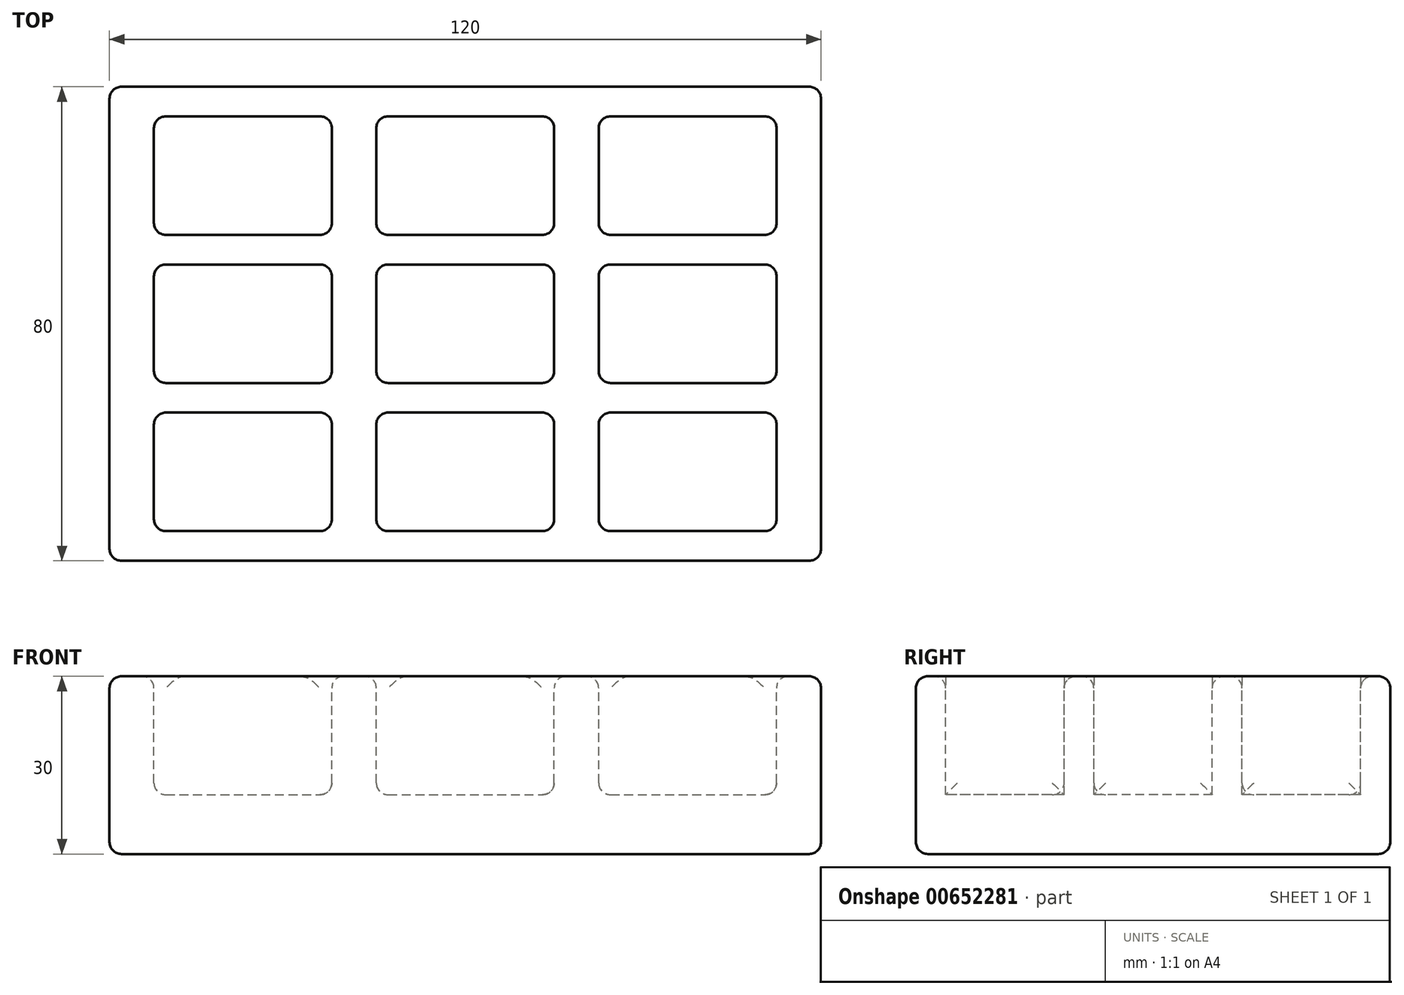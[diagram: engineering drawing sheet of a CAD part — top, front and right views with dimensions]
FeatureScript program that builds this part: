
annotation { "Feature Type Name" : "Feature", "Feature Type Description" : "" }
export const myFeature = defineFeature(function(context is Context, id is Id, definition is map)
    precondition{}
    {
        {
            var Q0;
            Q0=qCreatedBy(makeId("Top.planeOp"),FACE);
            var sketch = newSketch(context, id + "F0", { "sketchPlane" : qUnion([Q0])});
            skLineSegment(sketch, "E0.bottom", {"start": v(60, -40) * mm, "end": v(-60, -40) * mm});
            skLineSegment(sketch, "E0.top", {"start": v(60, 40) * mm, "end": v(-60, 40) * mm});
            skLineSegment(sketch, "E0.left", {"start": v(60, -40) * mm, "end": v(60, 40) * mm});
            skLineSegment(sketch, "E0.right", {"start": v(-60, -40) * mm, "end": v(-60, 40) * mm});
            skPoint(sketch, "E0.middle", {"position": v(0, 0) * mm});
            skSolve(sketch);
        }
        {
            var Q0;
            Q0 = qSketchRegion(id + "F0", true);
            extrude(context, id + "F1", {"entities" : qUnion([Q0]), "depth" : 30 * mm, "offsetDistance" : 25 * mm});
        }
        {
            var Q0;
            Q0=makeQuery(id+"F1.opExtrude","CAP_FACE",FACE,{"disambiguationData":[OSD([sQuery(id+"F0.wireOp",EDGE,"E0.bottom"),sQuery(id+"F0.wireOp",EDGE,"E0.top"),sQuery(id+"F0.wireOp",EDGE,"E0.left"),sQuery(id+"F0.wireOp",EDGE,"E0.right")])],"isStart":false});
            var sketch = newSketch(context, id + "F2", { "sketchPlane" : qUnion([Q0])});
            skLineSegment(sketch, "E1.bottom", {"start": v(-52.5, 35) * mm, "end": v(-22.5, 35) * mm});
            skLineSegment(sketch, "E1.top", {"start": v(-52.5, 15) * mm, "end": v(-22.5, 15) * mm});
            skLineSegment(sketch, "E1.left", {"start": v(-52.5, 35) * mm, "end": v(-52.5, 15) * mm});
            skLineSegment(sketch, "E1.right", {"start": v(-22.5, 35) * mm, "end": v(-22.5, 15) * mm});
            skLineSegment(sketch, "E2", {"start": v(-22.5, 35) * mm, "end": v(60, 35) * mm, "construction": true});
            skLineSegment(sketch, "E3", {"start": v(-22.5, -40) * mm, "end": v(-22.5, 35) * mm, "construction": true});
            skLineSegment(sketch, "E4", {"start": v(-22.5, 15) * mm, "end": v(60, 15) * mm, "construction": true});
            skLineSegment(sketch, "E5", {"start": v(-15, 35) * mm, "end": v(-15, -40) * mm, "construction": true});
            skLineSegment(sketch, "E6", {"start": v(52.5, 35) * mm, "end": v(52.5, -40) * mm, "construction": true});
            skLineSegment(sketch, "E7.bottom", {"start": v(-15, 35) * mm, "end": v(15, 35) * mm});
            skLineSegment(sketch, "E7.top", {"start": v(-15, 15) * mm, "end": v(15, 15) * mm});
            skLineSegment(sketch, "E7.left", {"start": v(-15, 35) * mm, "end": v(-15, 15) * mm});
            skLineSegment(sketch, "E7.right", {"start": v(15, 35) * mm, "end": v(15, 15) * mm});
            skLineSegment(sketch, "E8.bottom", {"start": v(52.5, 35) * mm, "end": v(22.5, 35) * mm});
            skLineSegment(sketch, "E8.top", {"start": v(52.5, 15) * mm, "end": v(22.5, 15) * mm});
            skLineSegment(sketch, "E8.left", {"start": v(52.5, 35) * mm, "end": v(52.5, 15) * mm});
            skLineSegment(sketch, "E8.right", {"start": v(22.5, 35) * mm, "end": v(22.5, 15) * mm});
            skLineSegment(sketch, "E9", {"start": v(-60, 10) * mm, "end": v(60, 10) * mm, "construction": true});
            skLineSegment(sketch, "E10", {"start": v(-52.5, 15) * mm, "end": v(-52.5, -40) * mm, "construction": true});
            skLineSegment(sketch, "E11", {"start": v(-60, -10) * mm, "end": v(60, -10) * mm, "construction": true});
            skLineSegment(sketch, "E12", {"start": v(15, 15) * mm, "end": v(15, -40) * mm, "construction": true});
            skLineSegment(sketch, "E13", {"start": v(22.5, 15) * mm, "end": v(22.5, -40) * mm, "construction": true});
            skLineSegment(sketch, "E14", {"start": v(60, -15) * mm, "end": v(-60, -15) * mm, "construction": true});
            skLineSegment(sketch, "E15", {"start": v(-60, -35) * mm, "end": v(60, -35) * mm, "construction": true});
            skLineSegment(sketch, "E16.bottom", {"start": v(-52.5, 10) * mm, "end": v(-22.5, 10) * mm});
            skLineSegment(sketch, "E16.top", {"start": v(-52.5, -10) * mm, "end": v(-22.5, -10) * mm});
            skLineSegment(sketch, "E16.left", {"start": v(-52.5, 10) * mm, "end": v(-52.5, -10) * mm});
            skLineSegment(sketch, "E16.right", {"start": v(-22.5, 10) * mm, "end": v(-22.5, -10) * mm});
            skPoint(sketch, "E17.oppositeSnap0", {"position": v(15, -12.5) * mm});
            skLineSegment(sketch, "E17.bottom", {"start": v(-15, 10) * mm, "end": v(15, 10) * mm});
            skLineSegment(sketch, "E17.top", {"start": v(-15, -10) * mm, "end": v(15, -10) * mm});
            skLineSegment(sketch, "E17.left", {"start": v(-15, 10) * mm, "end": v(-15, -10) * mm});
            skLineSegment(sketch, "E17.right", {"start": v(15, 10) * mm, "end": v(15, -10) * mm});
            skLineSegment(sketch, "E18.bottom", {"start": v(-52.5, -15) * mm, "end": v(-22.5, -15) * mm});
            skLineSegment(sketch, "E18.top", {"start": v(-52.5, -35) * mm, "end": v(-22.5, -35) * mm});
            skLineSegment(sketch, "E18.left", {"start": v(-52.5, -15) * mm, "end": v(-52.5, -35) * mm});
            skLineSegment(sketch, "E18.right", {"start": v(-22.5, -15) * mm, "end": v(-22.5, -35) * mm});
            skLineSegment(sketch, "E19.bottom", {"start": v(-15, -15) * mm, "end": v(15, -15) * mm});
            skLineSegment(sketch, "E19.top", {"start": v(-15, -35) * mm, "end": v(15, -35) * mm});
            skLineSegment(sketch, "E19.left", {"start": v(-15, -15) * mm, "end": v(-15, -35) * mm});
            skLineSegment(sketch, "E19.right", {"start": v(15, -15) * mm, "end": v(15, -35) * mm});
            skLineSegment(sketch, "E20.bottom", {"start": v(22.5, -15) * mm, "end": v(52.5, -15) * mm});
            skLineSegment(sketch, "E20.top", {"start": v(22.5, -35) * mm, "end": v(52.5, -35) * mm});
            skLineSegment(sketch, "E20.left", {"start": v(22.5, -15) * mm, "end": v(22.5, -35) * mm});
            skLineSegment(sketch, "E20.right", {"start": v(52.5, -15) * mm, "end": v(52.5, -35) * mm});
            skLineSegment(sketch, "E21.bottom", {"start": v(52.5, -10) * mm, "end": v(22.5, -10) * mm});
            skLineSegment(sketch, "E21.top", {"start": v(52.5, 10) * mm, "end": v(22.5, 10) * mm});
            skLineSegment(sketch, "E21.left", {"start": v(52.5, -10) * mm, "end": v(52.5, 10) * mm});
            skLineSegment(sketch, "E21.right", {"start": v(22.5, -10) * mm, "end": v(22.5, 10) * mm});
            skSolve(sketch);
        }
        {
            var Q0;
            Q0=makeQuery(id+"F2.imprint","IMPRINT",FACE,{"disambiguationData":[TD([[makeQuery(id+"F2.imprint","IMPRINT",EDGE,{"derivedFrom":sQuery(id+"F2.wireOp",EDGE,"E1.bottom")}),-1.0]])]});
            var Q1;
            Q1=makeQuery(id+"F2.imprint","IMPRINT",FACE,{"disambiguationData":[TD([[makeQuery(id+"F2.imprint","IMPRINT",EDGE,{"derivedFrom":sQuery(id+"F2.wireOp",EDGE,"E7.bottom")}),-1.0]])]});
            var Q2;
            Q2=makeQuery(id+"F2.imprint","IMPRINT",FACE,{"disambiguationData":[TD([[makeQuery(id+"F2.imprint","IMPRINT",EDGE,{"derivedFrom":sQuery(id+"F2.wireOp",EDGE,"E8.bottom")}),1.0]])]});
            var Q3;
            Q3=makeQuery(id+"F2.imprint","IMPRINT",FACE,{"disambiguationData":[TD([[makeQuery(id+"F2.imprint","IMPRINT",EDGE,{"derivedFrom":sQuery(id+"F2.wireOp",EDGE,"E21.bottom")}),-1.0]])]});
            var Q4;
            Q4=makeQuery(id+"F2.imprint","IMPRINT",FACE,{"disambiguationData":[TD([[makeQuery(id+"F2.imprint","IMPRINT",EDGE,{"derivedFrom":sQuery(id+"F2.wireOp",EDGE,"E17.bottom")}),-1.0]])]});
            var Q5;
            Q5=makeQuery(id+"F2.imprint","IMPRINT",FACE,{"disambiguationData":[TD([[makeQuery(id+"F2.imprint","IMPRINT",EDGE,{"derivedFrom":sQuery(id+"F2.wireOp",EDGE,"E16.bottom")}),-1.0]])]});
            var Q6;
            Q6=makeQuery(id+"F2.imprint","IMPRINT",FACE,{"disambiguationData":[TD([[makeQuery(id+"F2.imprint","IMPRINT",EDGE,{"derivedFrom":sQuery(id+"F2.wireOp",EDGE,"E18.bottom")}),-1.0]])]});
            var Q7;
            Q7=makeQuery(id+"F2.imprint","IMPRINT",FACE,{"disambiguationData":[TD([[makeQuery(id+"F2.imprint","IMPRINT",EDGE,{"derivedFrom":sQuery(id+"F2.wireOp",EDGE,"E19.bottom")}),-1.0]])]});
            var Q8;
            Q8=makeQuery(id+"F2.imprint","IMPRINT",FACE,{"disambiguationData":[TD([[makeQuery(id+"F2.imprint","IMPRINT",EDGE,{"derivedFrom":sQuery(id+"F2.wireOp",EDGE,"E20.bottom")}),-1.0]])]});
            extrude(context, id + "F3", {"entities" : qUnion([Q0, Q1, Q2, Q3, Q4, Q5, Q6, Q7, Q8]), "operationType" : NewBodyOperationType.REMOVE, "oppositeDirection" : true, "depth" : 20 * mm, "offsetDistance" : 25 * mm});
        }
        {
            var Q0;
            Q0=makeQuery(id+"F3.boolean.opBoolean","COPY",FACE,{"derivedFrom":makeQuery(id+"F3.opExtrude","CAP_FACE",FACE,{"disambiguationData":[OSD([sQuery(id+"F2.wireOp",EDGE,"E1.bottom"),sQuery(id+"F2.wireOp",EDGE,"E1.top"),sQuery(id+"F2.wireOp",EDGE,"E1.left"),sQuery(id+"F2.wireOp",EDGE,"E1.right")])],"isStart":false})});
            var Q1;
            Q1=makeQuery(id+"F3.boolean.opBoolean","COPY",FACE,{"derivedFrom":makeQuery(id+"F3.opExtrude","SWEPT_FACE",FACE,{"disambiguationData":[OSD([sQuery(id+"F2.wireOp",EDGE,"E1.left")])]})});
            var Q2;
            Q2=makeQuery(id+"F3.boolean.opBoolean","COPY",FACE,{"derivedFrom":makeQuery(id+"F3.opExtrude","SWEPT_FACE",FACE,{"disambiguationData":[OSD([sQuery(id+"F2.wireOp",EDGE,"E1.bottom")])]})});
            var Q3;
            Q3=makeQuery(id+"F3.boolean.opBoolean","COPY",FACE,{"derivedFrom":makeQuery(id+"F3.opExtrude","SWEPT_FACE",FACE,{"disambiguationData":[OSD([sQuery(id+"F2.wireOp",EDGE,"E1.top")])]})});
            var Q4;
            Q4=makeQuery(id+"F3.boolean.opBoolean","COPY",FACE,{"derivedFrom":makeQuery(id+"F3.opExtrude","SWEPT_FACE",FACE,{"disambiguationData":[OSD([sQuery(id+"F2.wireOp",EDGE,"E1.right")])]})});
            var Q5;
            Q5=makeQuery(id+"F3.boolean.opBoolean","COPY",FACE,{"derivedFrom":makeQuery(id+"F3.opExtrude","SWEPT_FACE",FACE,{"disambiguationData":[OSD([sQuery(id+"F2.wireOp",EDGE,"E7.left")])]})});
            var Q6;
            Q6=makeQuery(id+"F3.boolean.opBoolean","COPY",FACE,{"derivedFrom":makeQuery(id+"F3.opExtrude","SWEPT_FACE",FACE,{"disambiguationData":[OSD([sQuery(id+"F2.wireOp",EDGE,"E7.right")])]})});
            var Q7;
            Q7=makeQuery(id+"F3.boolean.opBoolean","COPY",FACE,{"derivedFrom":makeQuery(id+"F3.opExtrude","SWEPT_FACE",FACE,{"disambiguationData":[OSD([sQuery(id+"F2.wireOp",EDGE,"E8.right")])]})});
            var Q8;
            Q8=makeQuery(id+"F3.boolean.opBoolean","COPY",FACE,{"derivedFrom":makeQuery(id+"F3.opExtrude","SWEPT_FACE",FACE,{"disambiguationData":[OSD([sQuery(id+"F2.wireOp",EDGE,"E8.left")])]})});
            var Q9;
            Q9=makeQuery(id+"F3.boolean.opBoolean","COPY",FACE,{"derivedFrom":makeQuery(id+"F3.opExtrude","SWEPT_FACE",FACE,{"disambiguationData":[OSD([sQuery(id+"F2.wireOp",EDGE,"E16.right")])]})});
            var Q10;
            Q10=makeQuery(id+"F3.boolean.opBoolean","COPY",FACE,{"derivedFrom":makeQuery(id+"F3.opExtrude","SWEPT_FACE",FACE,{"disambiguationData":[OSD([sQuery(id+"F2.wireOp",EDGE,"E19.right")])]})});
            var Q11;
            Q11=makeQuery(id+"F3.boolean.opBoolean","COPY",FACE,{"derivedFrom":makeQuery(id+"F3.opExtrude","SWEPT_FACE",FACE,{"disambiguationData":[OSD([sQuery(id+"F2.wireOp",EDGE,"E17.right")])]})});
            var Q12;
            Q12=makeQuery(id+"F3.boolean.opBoolean","COPY",FACE,{"derivedFrom":makeQuery(id+"F3.opExtrude","SWEPT_FACE",FACE,{"disambiguationData":[OSD([sQuery(id+"F2.wireOp",EDGE,"E17.top")])]})});
            var Q13;
            Q13=makeQuery(id+"F3.boolean.opBoolean","COPY",FACE,{"derivedFrom":makeQuery(id+"F3.opExtrude","SWEPT_FACE",FACE,{"disambiguationData":[OSD([sQuery(id+"F2.wireOp",EDGE,"E17.left")])]})});
            var Q14;
            Q14=makeQuery(id+"F3.boolean.opBoolean","COPY",FACE,{"derivedFrom":makeQuery(id+"F3.opExtrude","SWEPT_FACE",FACE,{"disambiguationData":[OSD([sQuery(id+"F2.wireOp",EDGE,"E16.left")])]})});
            var Q15;
            Q15=makeQuery(id+"F3.boolean.opBoolean","COPY",FACE,{"derivedFrom":makeQuery(id+"F3.opExtrude","SWEPT_FACE",FACE,{"disambiguationData":[OSD([sQuery(id+"F2.wireOp",EDGE,"E18.left")])]})});
            var Q16;
            Q16=makeQuery(id+"F3.boolean.opBoolean","COPY",FACE,{"derivedFrom":makeQuery(id+"F3.opExtrude","SWEPT_FACE",FACE,{"disambiguationData":[OSD([sQuery(id+"F2.wireOp",EDGE,"E19.left")])]})});
            var Q17;
            Q17=makeQuery(id+"F3.boolean.opBoolean","COPY",FACE,{"derivedFrom":makeQuery(id+"F3.opExtrude","SWEPT_FACE",FACE,{"disambiguationData":[OSD([sQuery(id+"F2.wireOp",EDGE,"E20.left")])]})});
            var Q18;
            Q18=makeQuery(id+"F3.boolean.opBoolean","COPY",FACE,{"derivedFrom":makeQuery(id+"F3.opExtrude","SWEPT_FACE",FACE,{"disambiguationData":[OSD([sQuery(id+"F2.wireOp",EDGE,"E21.right")])]})});
            var Q19;
            Q19=makeQuery(id+"F3.boolean.opBoolean","COPY",FACE,{"derivedFrom":makeQuery(id+"F3.opExtrude","SWEPT_FACE",FACE,{"disambiguationData":[OSD([sQuery(id+"F2.wireOp",EDGE,"E20.bottom")])]})});
            var Q20;
            Q20=makeQuery(id+"F3.boolean.opBoolean","COPY",FACE,{"derivedFrom":makeQuery(id+"F3.opExtrude","SWEPT_FACE",FACE,{"disambiguationData":[OSD([sQuery(id+"F2.wireOp",EDGE,"E20.right")])]})});
            var Q21;
            Q21=makeQuery(id+"F3.boolean.opBoolean","COPY",FACE,{"derivedFrom":makeQuery(id+"F3.opExtrude","SWEPT_FACE",FACE,{"disambiguationData":[OSD([sQuery(id+"F2.wireOp",EDGE,"E21.left")])]})});
            var Q22;
            Q22=makeQuery(id+"F3.boolean.opBoolean","COPY",FACE,{"derivedFrom":makeQuery(id+"F3.opExtrude","SWEPT_FACE",FACE,{"disambiguationData":[OSD([sQuery(id+"F2.wireOp",EDGE,"E18.right")])]})});
            var Q23;
            Q23=makeQuery(id+"F1.opExtrude","SWEPT_EDGE",EDGE,{"disambiguationData":[OSD([sQuery(id+"F0.wireOp",EDGE,"E0.top"),sQuery(id+"F0.wireOp",EDGE,"E0.right")])]});
            var Q24;
            Q24=makeQuery(id+"F1.opExtrude","SWEPT_EDGE",EDGE,{"disambiguationData":[OSD([sQuery(id+"F0.wireOp",EDGE,"E0.bottom"),sQuery(id+"F0.wireOp",EDGE,"E0.right")])]});
            var Q25;
            Q25=makeQuery(id+"F1.opExtrude","SWEPT_FACE",FACE,{"disambiguationData":[OSD([sQuery(id+"F0.wireOp",EDGE,"E0.bottom")])]});
            var Q26;
            Q26=makeQuery(id+"F1.opExtrude","SWEPT_FACE",FACE,{"disambiguationData":[OSD([sQuery(id+"F0.wireOp",EDGE,"E0.left")])]});
            var Q27;
            Q27=makeQuery(id+"F1.opExtrude","SWEPT_FACE",FACE,{"disambiguationData":[OSD([sQuery(id+"F0.wireOp",EDGE,"E0.right")])]});
            var Q28;
            Q28=makeQuery(id+"F1.opExtrude","SWEPT_FACE",FACE,{"disambiguationData":[OSD([sQuery(id+"F0.wireOp",EDGE,"E0.top")])]});
            fillet(context, id + "F4", {"entities" : qUnion([Q0, Q1, Q2, Q3, Q4, Q5, Q6, Q7, Q8, Q9, Q10, Q11, Q12, Q13, Q14, Q15, Q16, Q17, Q18, Q19, Q20, Q21, Q22, Q23, Q24, Q25, Q26, Q27, Q28]), "radius" : 2 * mm, "tangentPropagation" : true, "allowEdgeOverflow" : false});
        }
    });
